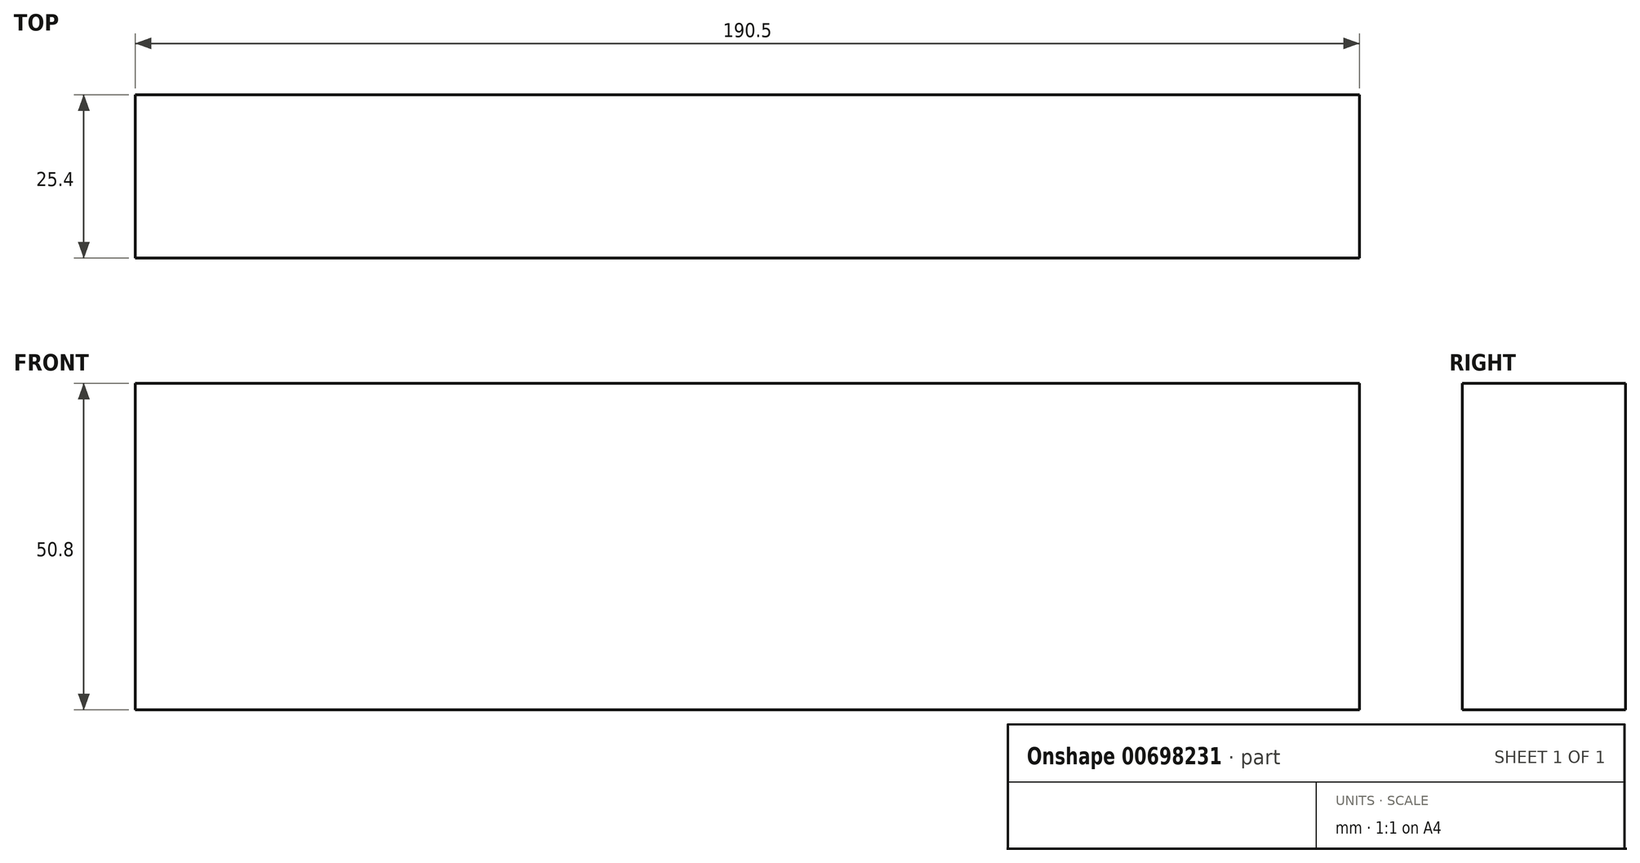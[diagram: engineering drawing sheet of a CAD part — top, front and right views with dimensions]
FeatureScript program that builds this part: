
annotation { "Feature Type Name" : "Feature", "Feature Type Description" : "" }
export const myFeature = defineFeature(function(context is Context, id is Id, definition is map)
    precondition{}
    {
        {
            var Q0;
            Q0=qCreatedBy(makeId("Front.planeOp"),FACE);
            var sketch = newSketch(context, id + "F0", { "sketchPlane" : qUnion([Q0])});
            skLineSegment(sketch, "E0.bottom", {"start": v(-84, 6) * mm, "end": v(106.5, 6) * mm});
            skLineSegment(sketch, "E0.top", {"start": v(-84, -44.8) * mm, "end": v(106.5, -44.8) * mm});
            skLineSegment(sketch, "E0.left", {"start": v(-84, 6) * mm, "end": v(-84, -44.8) * mm});
            skLineSegment(sketch, "E0.right", {"start": v(106.5, 6) * mm, "end": v(106.5, -44.8) * mm});
            skSolve(sketch);
        }
        {
            var Q0;
            Q0=makeQuery(id+"F0.imprint","IMPRINT",FACE,{"disambiguationData":[TD([[makeQuery(id+"F0.imprint","IMPRINT",EDGE,{"derivedFrom":sQuery(id+"F0.wireOp",EDGE,"E0.bottom")}),-1.0]])]});
            extrude(context, id + "F1", {"entities" : qUnion([Q0]), "depth" : 25.4 * mm, "offsetDistance" : 25.4 * mm});
        }
    });
